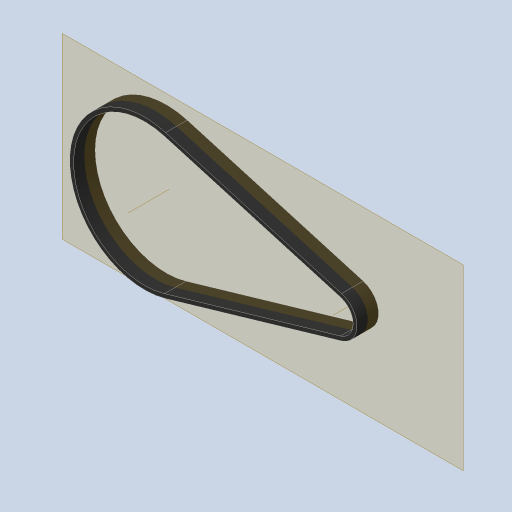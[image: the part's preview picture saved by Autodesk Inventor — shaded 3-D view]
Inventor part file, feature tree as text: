
AUTODESK INVENTOR PART (.ipt)
format: ipt  version: 2023.4 (Build 274418000, 418)  size: 173,568 bytes
history: native  units: in
note: dims shown in document units (in); Inventor stores cm internally (conversion verified against a paired STEP export)
features: sketch x3, extrude x1, other x1, projected_geometry x1
ambient origin geometry x8: Origin, YZ Plane, XZ Plane, XY Plane, X Axis, Y Axis, Z Axis, Center Point
bodies: Body1 (feature_tree)
feature tree (6):
  sketch  "Sketch2"  dims[d0=0.6015in d1=2.2558in]
  extrude  "Extrusion2"  Depth=2.2558in
  sketch  "Sketch5"  dims[d3=4.1836in d5=2.8361in d9=0.0787in d10=0.0598in d11=0.0299in d12=0.0219in d13=0.0219in d14=0.0059in d15=0.0059in d20=0.3346in d21=0.0in d22=0.0787in d23=0.0598in d24=0.0299in d25=0.0219in d26=0.0219in d27=0.0059in d28=0.0059in d29=0.0299in d30=0.0394in d31=0.0787in d32=0.0232in d34=0.0219in d35=0.0in d36=0.0in d37=0.0059in d38=0.0022in d39=0.0022in d40=0.0in d41=0.0in d42=0.0081in d43=0.0081in d44=0.0299in]
  other  "Work Axis1"
  sketch  "Sketch4"  dims[d2=0.7742in]
  projected_geometry  "Projected Loop1"
